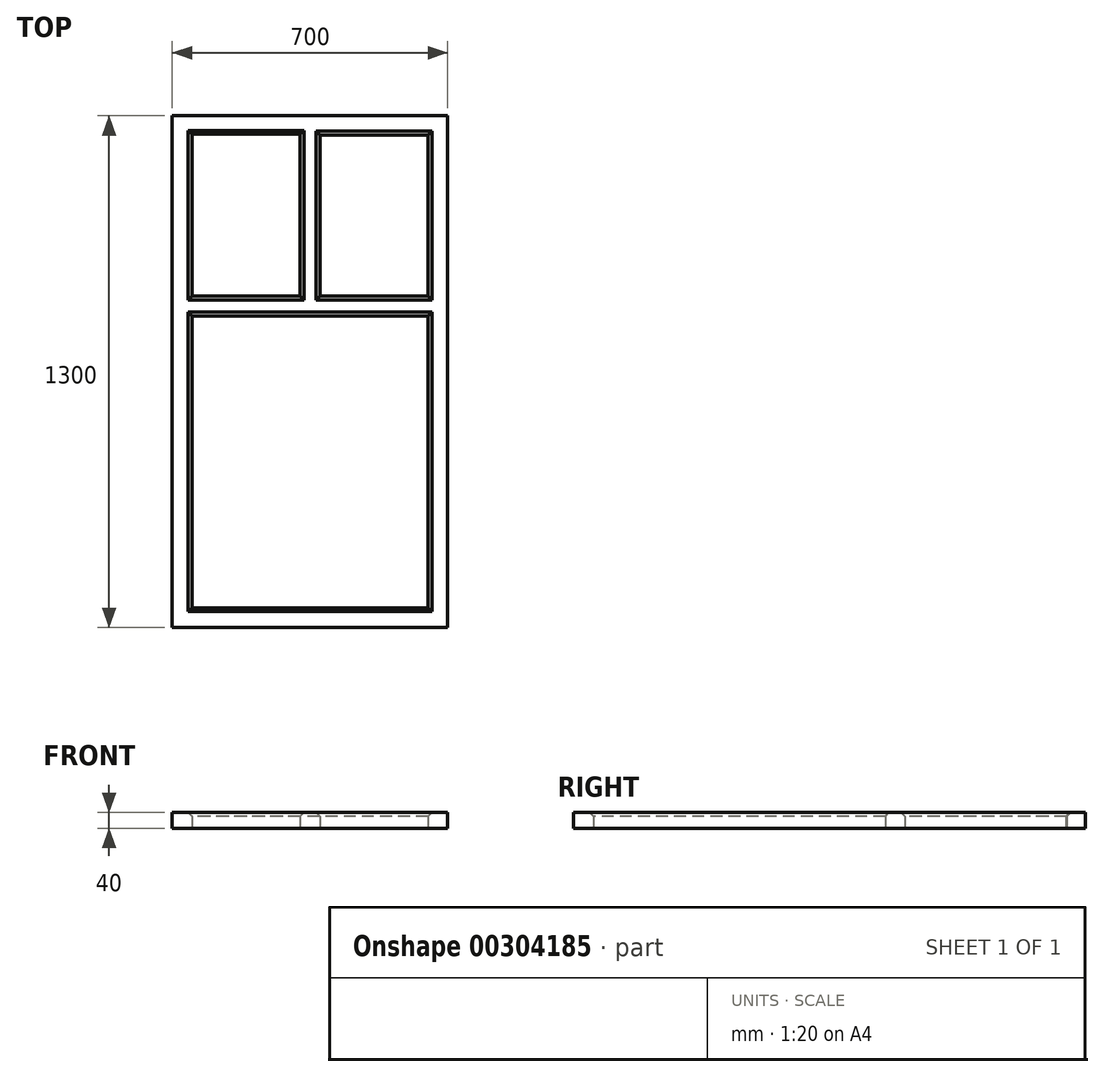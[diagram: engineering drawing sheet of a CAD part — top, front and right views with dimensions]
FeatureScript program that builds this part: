
annotation { "Feature Type Name" : "Feature", "Feature Type Description" : "" }
export const myFeature = defineFeature(function(context is Context, id is Id, definition is map)
    precondition{}
    {
        {
            var Q0;
            Q0=qCreatedBy(makeId("Top.planeOp"),FACE);
            var sketch = newSketch(context, id + "F0", { "sketchPlane" : qUnion([Q0])});
            skLineSegment(sketch, "E0.bottom", {"start": v(-351.15, 792.79) * mm, "end": v(348.85, 792.79) * mm});
            skLineSegment(sketch, "E0.top", {"start": v(-351.15, -507.21) * mm, "end": v(348.85, -507.21) * mm});
            skLineSegment(sketch, "E0.left", {"start": v(-351.15, 792.79) * mm, "end": v(-351.15, -507.21) * mm});
            skLineSegment(sketch, "E0.right", {"start": v(348.85, 792.79) * mm, "end": v(348.85, -507.21) * mm});
            skLineSegment(sketch, "E1.bottom", {"start": v(-301.15, 745.65) * mm, "end": v(-26.15, 745.65) * mm});
            skLineSegment(sketch, "E1.top", {"start": v(-301.15, 334.15) * mm, "end": v(-26.15, 334.15) * mm});
            skLineSegment(sketch, "E1.left", {"start": v(-301.15, 745.65) * mm, "end": v(-301.15, 334.15) * mm});
            skLineSegment(sketch, "E1.right", {"start": v(-26.15, 745.65) * mm, "end": v(-26.15, 334.15) * mm});
            skLineSegment(sketch, "E2.bottom", {"start": v(23.85, 743.43) * mm, "end": v(298.85, 743.43) * mm});
            skLineSegment(sketch, "E2.top", {"start": v(23.85, 334.15) * mm, "end": v(298.85, 334.15) * mm});
            skLineSegment(sketch, "E2.left", {"start": v(23.85, 743.43) * mm, "end": v(23.85, 334.15) * mm});
            skLineSegment(sketch, "E2.right", {"start": v(298.85, 743.43) * mm, "end": v(298.85, 334.15) * mm});
            skLineSegment(sketch, "E3.bottom", {"start": v(-301.15, 284.15) * mm, "end": v(298.85, 284.15) * mm});
            skLineSegment(sketch, "E3.top", {"start": v(-301.15, -457.21) * mm, "end": v(298.85, -457.21) * mm});
            skLineSegment(sketch, "E3.left", {"start": v(-301.15, 284.15) * mm, "end": v(-301.15, -457.21) * mm});
            skLineSegment(sketch, "E3.right", {"start": v(298.85, 284.15) * mm, "end": v(298.85, -457.21) * mm});
            skSolve(sketch);
        }
        {
            var Q0;
            Q0=makeQuery(id+"F0.imprint","IMPRINT",FACE,{"disambiguationData":[TD([[makeQuery(id+"F0.imprint","IMPRINT",EDGE,{"derivedFrom":sQuery(id+"F0.wireOp",EDGE,"E0.bottom")}),-1.0]])]});
            extrude(context, id + "F1", {"entities" : qUnion([Q0]), "depth" : 40 * mm});
        }
        {
            var Q0;
            Q0=makeQuery(id+"F1.opExtrude","CAP_EDGE",EDGE,{"disambiguationData":[OSD([sQuery(id+"F0.wireOp",EDGE,"E3.top")])],"isStart":false});
            var Q1;
            Q1=makeQuery(id+"F1.opExtrude","CAP_EDGE",EDGE,{"disambiguationData":[OSD([sQuery(id+"F0.wireOp",EDGE,"E3.right")])],"isStart":false});
            var Q2;
            Q2=makeQuery(id+"F1.opExtrude","CAP_EDGE",EDGE,{"disambiguationData":[OSD([sQuery(id+"F0.wireOp",EDGE,"E3.bottom")])],"isStart":false});
            var Q3;
            Q3=makeQuery(id+"F1.opExtrude","CAP_EDGE",EDGE,{"disambiguationData":[OSD([sQuery(id+"F0.wireOp",EDGE,"E3.left")])],"isStart":false});
            var Q4;
            Q4=makeQuery(id+"F1.opExtrude","CAP_EDGE",EDGE,{"disambiguationData":[OSD([sQuery(id+"F0.wireOp",EDGE,"E2.left")])],"isStart":false});
            var Q5;
            Q5=makeQuery(id+"F1.opExtrude","CAP_EDGE",EDGE,{"disambiguationData":[OSD([sQuery(id+"F0.wireOp",EDGE,"E2.top")])],"isStart":false});
            var Q6;
            Q6=makeQuery(id+"F1.opExtrude","CAP_EDGE",EDGE,{"disambiguationData":[OSD([sQuery(id+"F0.wireOp",EDGE,"E1.top")])],"isStart":false});
            var Q7;
            Q7=makeQuery(id+"F1.opExtrude","CAP_EDGE",EDGE,{"disambiguationData":[OSD([sQuery(id+"F0.wireOp",EDGE,"E1.right")])],"isStart":false});
            var Q8;
            Q8=makeQuery(id+"F1.opExtrude","CAP_EDGE",EDGE,{"disambiguationData":[OSD([sQuery(id+"F0.wireOp",EDGE,"E2.right")])],"isStart":false});
            var Q9;
            Q9=makeQuery(id+"F1.opExtrude","CAP_EDGE",EDGE,{"disambiguationData":[OSD([sQuery(id+"F0.wireOp",EDGE,"E1.left")])],"isStart":false});
            var Q10;
            Q10=makeQuery(id+"F1.opExtrude","CAP_EDGE",EDGE,{"disambiguationData":[OSD([sQuery(id+"F0.wireOp",EDGE,"E1.bottom")])],"isStart":false});
            var Q11;
            Q11=makeQuery(id+"F1.opExtrude","CAP_EDGE",EDGE,{"disambiguationData":[OSD([sQuery(id+"F0.wireOp",EDGE,"E2.bottom")])],"isStart":false});
            chamfer(context, id + "F2", {"entities" : qUnion([Q0, Q1, Q2, Q3, Q4, Q5, Q6, Q7, Q8, Q9, Q10, Q11]), "width" : 10 * mm, "tangentPropagation" : true});
        }
    });
